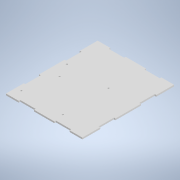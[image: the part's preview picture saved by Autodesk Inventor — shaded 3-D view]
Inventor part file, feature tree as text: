
AUTODESK INVENTOR PART (.ipt)
format: ipt  version: 2020.3 (Build 243373000, 373)  size: 173,056 bytes
history: native  units: mm
features: extrude x3, sketch x2, other x1
ambient origin geometry x8: Origin, YZ Plane, XZ Plane, XY Plane, X Axis, Y Axis, Z Axis, Center Point
bodies: Solid1 (feature_tree)
feature tree (6):
  extrude  "Baseplate"  Depth=150.0mm
  extrude  "Extrusion2"  Depth=3.0mm
  extrude  "PCB Mounting"  Depth=35.0mm
  sketch  "Sketch1"  dims[d0=180.0mm d1=150.0mm]
  other  "TabsSketch"
  sketch  "Sketch3"  dims[d2=3.0mm d3=0.0mm d4=3.0mm d5=35.0mm d7=35.0mm d8=30.0mm d9=30.0mm d10=50.0mm d11=3.0mm d12=3.0mm d13=30.0mm d14=30.0mm d15=25.0mm d16=40.0mm d17=0.0mm d18=0.0mm d19=3.2mm d20=3.2mm d21=3.2mm d22=3.2mm d23=89.5mm d24=81.5mm d25=89.5mm d26=81.5mm d27=10.0mm d28=10.0mm d29=20.0mm d30=20.0mm d31=61.5mm d32=68.0mm d33=3.2mm d34=0.0mm d35=0.0mm]
